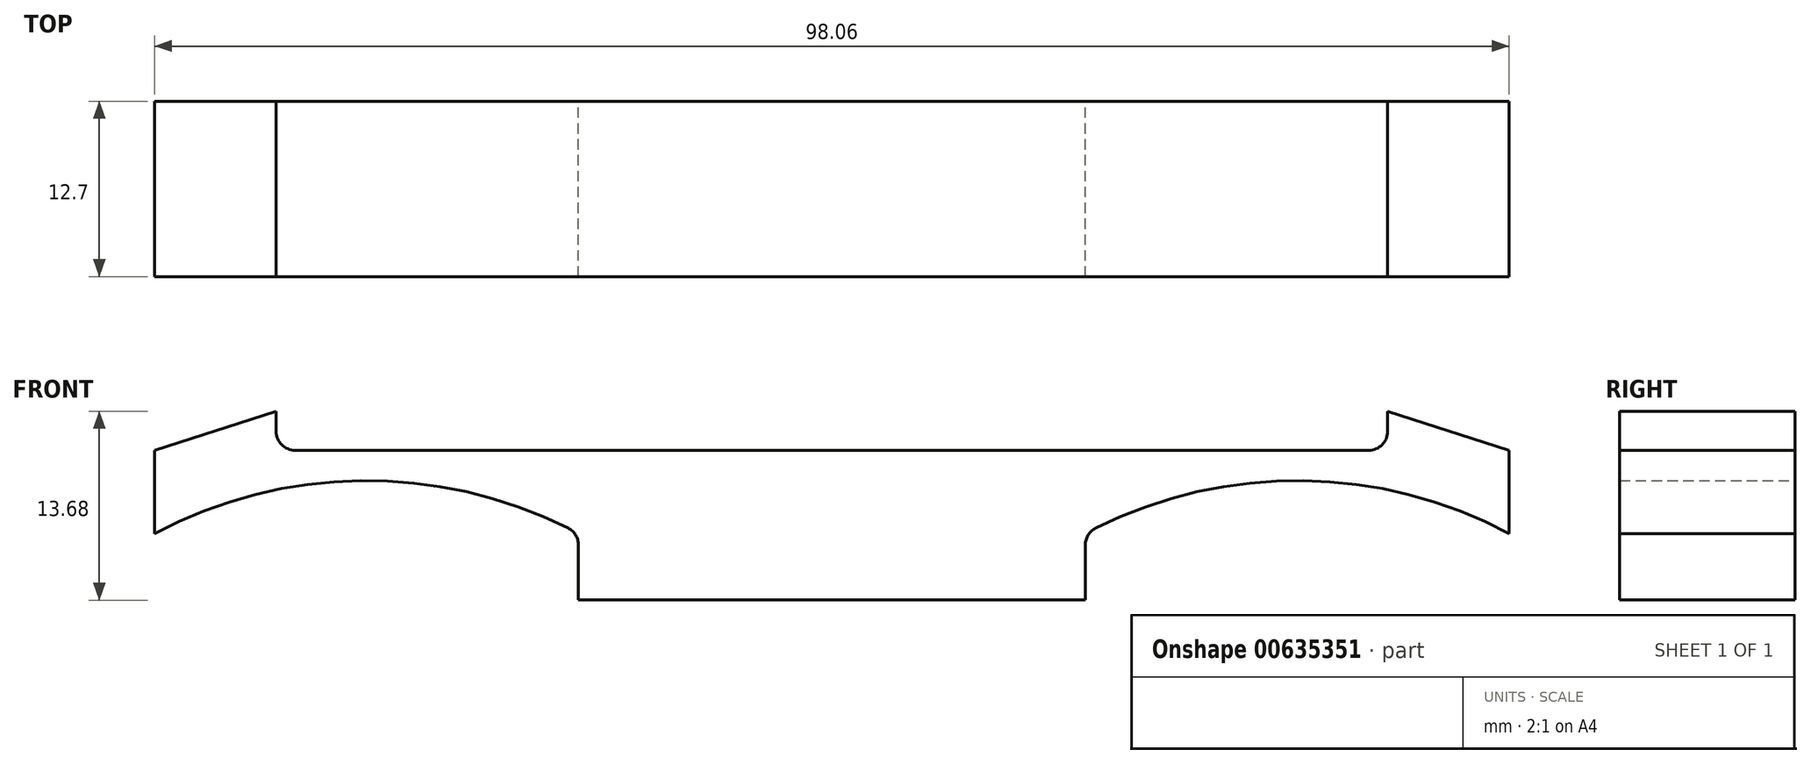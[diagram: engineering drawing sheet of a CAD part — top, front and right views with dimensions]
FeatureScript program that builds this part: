
annotation { "Feature Type Name" : "Feature", "Feature Type Description" : "" }
export const myFeature = defineFeature(function(context is Context, id is Id, definition is map)
    precondition{}
    {
        {
            var Q0;
            Q0=qCreatedBy(makeId("Front.planeOp"),FACE);
            var sketch = newSketch(context, id + "F0", { "sketchPlane" : qUnion([Q0])});
            skLineSegment(sketch, "E0", {"start": v(0, 0) * mm, "end": v(-38.86, 0) * mm});
            skLineSegment(sketch, "E1", {"start": v(-40.23, 1.36) * mm, "end": v(-40.23, 2.83) * mm});
            skLineSegment(sketch, "E2", {"start": v(-40.23, 2.83) * mm, "end": v(-49.03, 0) * mm});
            skLineSegment(sketch, "E3", {"start": v(-49.03, 0) * mm, "end": v(-49.03, -6.02) * mm});
            skArc(sketch, "E4", {"start": v(-19.1, -5.64) * mm, "mid": v(-34.11, -2.2) * mm, "end": v(-49.03, -6.02) * mm});
            skLineSegment(sketch, "E5", {"start": v(-18.35, -6.86) * mm, "end": v(-18.35, -10.85) * mm});
            skLineSegment(sketch, "E6", {"start": v(-18.35, -10.85) * mm, "end": v(0, -10.85) * mm});
            skLineSegment(sketch, "E7", {"start": v(0, -10.85) * mm, "end": v(0, 0) * mm});
            skPoint(sketch, "E8.visualSharp", {"position": v(-40.23, 0) * mm});
            skArc(sketch, "E8.filletArc", {"start": v(-40.23, 1.36) * mm, "mid": v(-39.83, 0.4) * mm, "end": v(-38.86, 0) * mm});
            skPoint(sketch, "E9.visualSharp", {"position": v(-18.35, -6.02) * mm});
            skArc(sketch, "E9.filletArc", {"start": v(-18.35, -6.86) * mm, "mid": v(-18.55, -6.14) * mm, "end": v(-19.1, -5.64) * mm});
            skLineSegment(sketch, "E10.MirrorCS", {"start": v(0, 0) * mm, "end": v(38.86, 0) * mm});
            skArc(sketch, "E11.MirrorCS", {"start": v(18.35, -6.86) * mm, "mid": v(18.55, -6.14) * mm, "end": v(19.1, -5.64) * mm});
            skArc(sketch, "E12.MirrorCS", {"start": v(40.23, 1.36) * mm, "mid": v(39.83, 0.4) * mm, "end": v(38.86, 0) * mm});
            skLineSegment(sketch, "E13.MirrorCS", {"start": v(40.23, 1.36) * mm, "end": v(40.23, 2.83) * mm});
            skPoint(sketch, "E14.MirrorP", {"position": v(18.35, -6.02) * mm});
            skPoint(sketch, "E15.MirrorP", {"position": v(40.23, 0) * mm});
            skLineSegment(sketch, "E16.MirrorCS", {"start": v(40.23, 2.83) * mm, "end": v(49.03, 0) * mm});
            skLineSegment(sketch, "E17.MirrorCS", {"start": v(49.03, 0) * mm, "end": v(49.03, -6.02) * mm});
            skArc(sketch, "E18.MirrorCS", {"start": v(19.1, -5.64) * mm, "mid": v(34.11, -2.2) * mm, "end": v(49.03, -6.02) * mm});
            skLineSegment(sketch, "E19.MirrorCS", {"start": v(18.35, -6.86) * mm, "end": v(18.35, -10.85) * mm});
            skLineSegment(sketch, "E20.MirrorCS", {"start": v(18.35, -10.85) * mm, "end": v(0, -10.85) * mm});
            skSolve(sketch);
        }
        {
            var Q0;
            Q0=makeQuery(id+"F0.imprint","IMPRINT",FACE,{"disambiguationData":[TD([[makeQuery(id+"F0.imprint","IMPRINT",EDGE,{"derivedFrom":sQuery(id+"F0.wireOp",EDGE,"E0")}),1.0]])]});
            var Q1;
            Q1=makeQuery(id+"F0.imprint","IMPRINT",FACE,{"disambiguationData":[TD([[makeQuery(id+"F0.imprint","IMPRINT",EDGE,{"derivedFrom":sQuery(id+"F0.wireOp",EDGE,"E7")}),-1.0]])]});
            extrude(context, id + "F1", {"entities" : qUnion([Q0, Q1]), "depth" : 12.7 * mm, "offsetDistance" : 25.4 * mm});
        }
    });
